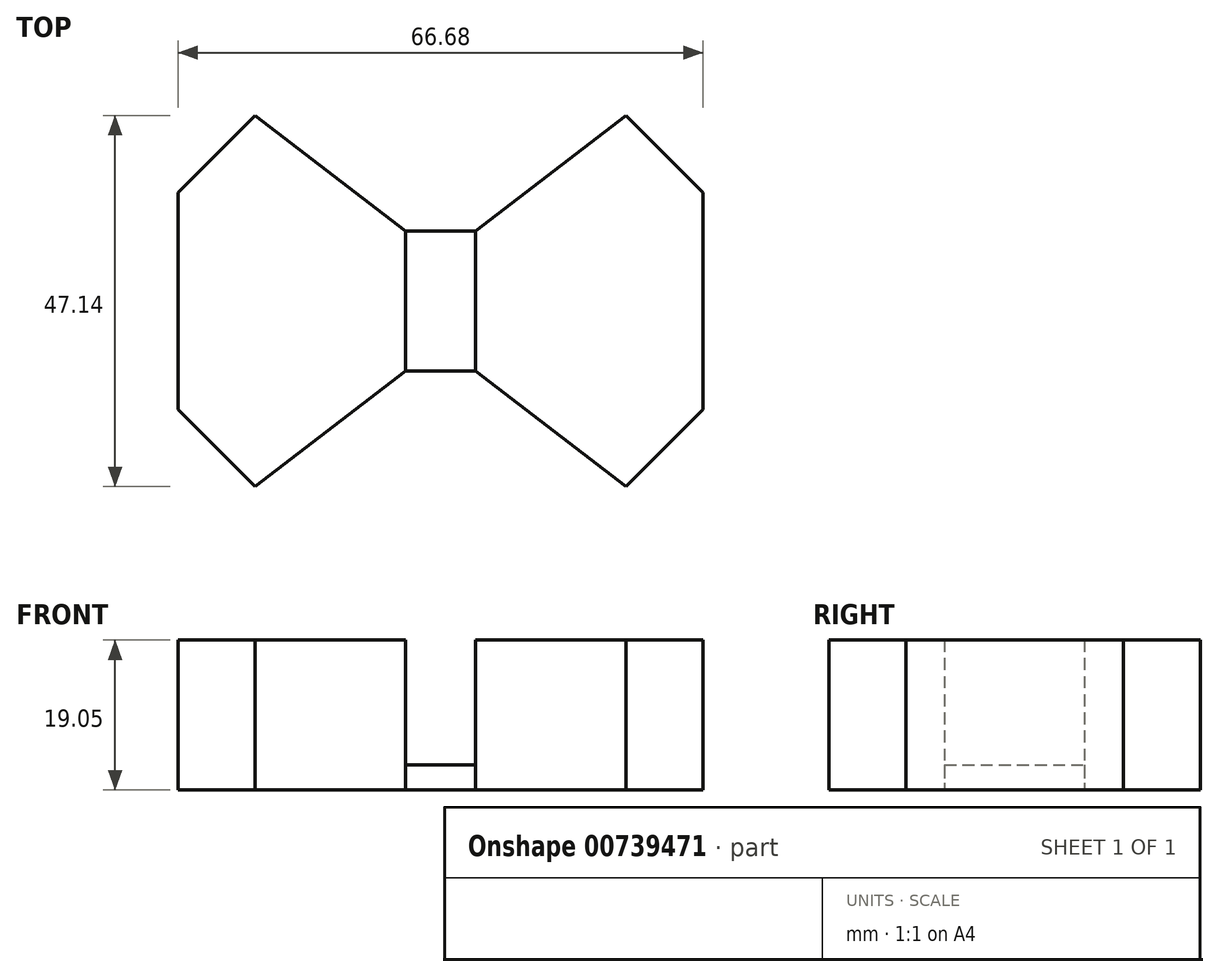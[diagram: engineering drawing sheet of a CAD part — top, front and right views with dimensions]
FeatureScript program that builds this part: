
annotation { "Feature Type Name" : "Feature", "Feature Type Description" : "" }
export const myFeature = defineFeature(function(context is Context, id is Id, definition is map)
    precondition{}
    {
        {
            var Q0;
            Q0=qCreatedBy(makeId("Top.planeOp"),FACE);
            var sketch = newSketch(context, id + "F0", { "sketchPlane" : qUnion([Q0])});
            skCircle(sketch, "E0.cCircle", {"center": v(0, 0) * mm, "radius": 33.34 * mm, "construction": true});
            skLineSegment(sketch, "E0.0", {"start": v(33.34, -13.8) * mm, "end": v(13.8, -33.34) * mm});
            skLineSegment(sketch, "E0.1", {"start": v(13.8, -33.34) * mm, "end": v(-13.8, -33.34) * mm});
            skLineSegment(sketch, "E0.2", {"start": v(-13.8, -33.34) * mm, "end": v(-33.34, -13.8) * mm});
            skLineSegment(sketch, "E0.3", {"start": v(-33.34, -13.8) * mm, "end": v(-33.34, 13.8) * mm});
            skLineSegment(sketch, "E0.4", {"start": v(-33.34, 13.8) * mm, "end": v(-13.8, 33.34) * mm});
            skLineSegment(sketch, "E0.5", {"start": v(-13.8, 33.34) * mm, "end": v(13.8, 33.34) * mm});
            skLineSegment(sketch, "E0.6", {"start": v(13.8, 33.34) * mm, "end": v(33.34, 13.8) * mm});
            skLineSegment(sketch, "E0.7", {"start": v(33.34, 13.8) * mm, "end": v(33.34, -13.8) * mm});
            skPoint(sketch, "E0.0.midPoint", {"position": v(23.57, -23.57) * mm});
            skLineSegment(sketch, "E1.bottom", {"start": v(4.44, -8.9) * mm, "end": v(-4.45, -8.9) * mm});
            skLineSegment(sketch, "E1.top", {"start": v(4.45, 8.9) * mm, "end": v(-4.44, 8.9) * mm});
            skLineSegment(sketch, "E1.left", {"start": v(4.44, -8.9) * mm, "end": v(4.45, 8.9) * mm});
            skLineSegment(sketch, "E1.right", {"start": v(-4.45, -8.9) * mm, "end": v(-4.44, 8.9) * mm});
            skLineSegment(sketch, "E2", {"start": v(23.57, 23.57) * mm, "end": v(4.44, 8.9) * mm});
            skLineSegment(sketch, "E3", {"start": v(23.57, -23.57) * mm, "end": v(4.44, -8.9) * mm});
            skLineSegment(sketch, "E4", {"start": v(-23.57, -23.57) * mm, "end": v(-4.44, -8.9) * mm});
            skLineSegment(sketch, "E5", {"start": v(-23.57, 23.57) * mm, "end": v(-4.44, 8.9) * mm});
            skSolve(sketch);
        }
        {
            var Q0;
            {var subQ0=sQuery(id+"F0.wireOp",EDGE,"E0.7");Q0=makeQuery(id+"F0.imprint","IMPRINT",FACE,{"disambiguationData":[TD([[makeQuery(id+"F0.imprint","IMPRINT",EDGE,{"derivedFrom":subQ0}),-1.0]])]});}
            var Q1;
            {var subQ1=sQuery(id+"F0.wireOp",EDGE,"E0.3");Q1=makeQuery(id+"F0.imprint","IMPRINT",FACE,{"disambiguationData":[TD([[makeQuery(id+"F0.imprint","IMPRINT",EDGE,{"derivedFrom":subQ1}),-1.0]])]});}
            extrude(context, id + "F1", {"entities" : qUnion([Q0, Q1]), "depth" : 19.05 * mm, "offsetDistance" : 25.4 * mm});
        }
        {
            var Q0;
            Q0=makeQuery(id+"F0.imprint","IMPRINT",FACE,{"disambiguationData":[TD([[makeQuery(id+"F0.imprint","IMPRINT",EDGE,{"derivedFrom":sQuery(id+"F0.wireOp",EDGE,"E1.bottom")}),-1.0]])]});
            extrude(context, id + "F2", {"entities" : qUnion([Q0]), "depth" : 3.17 * mm, "offsetDistance" : 25.4 * mm});
        }
    });
